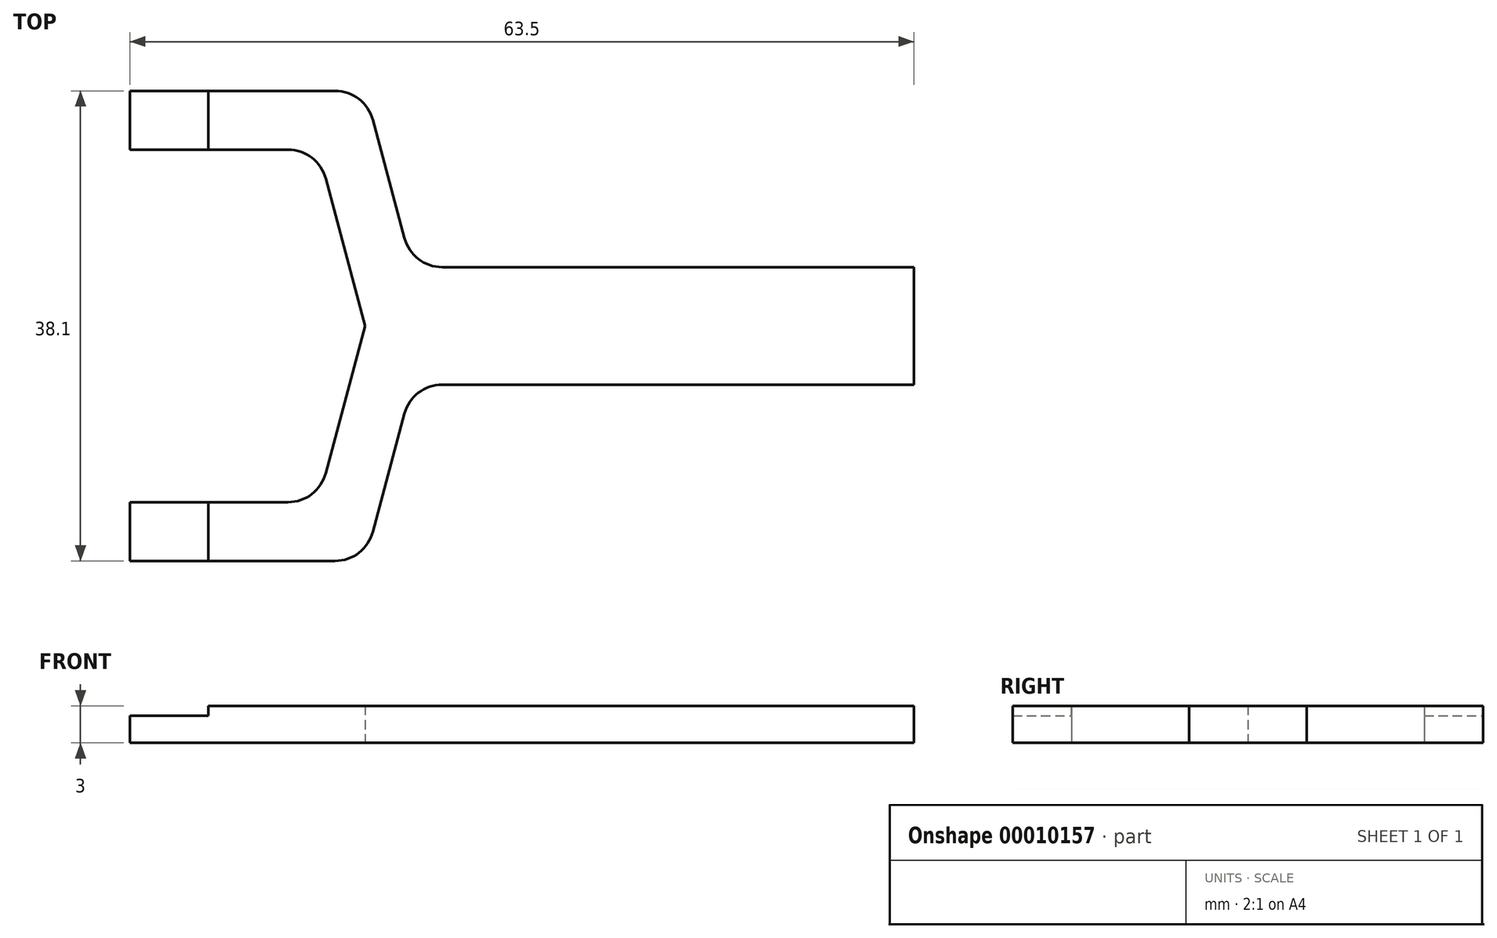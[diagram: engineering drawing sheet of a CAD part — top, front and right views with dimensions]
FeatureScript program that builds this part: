
annotation { "Feature Type Name" : "Feature", "Feature Type Description" : "" }
export const myFeature = defineFeature(function(context is Context, id is Id, definition is map)
    precondition{}
    {
        {
            var Q0;
            Q0=qCreatedBy(makeId("Top.planeOp"),FACE);
            var sketch = newSketch(context, id + "F0", { "sketchPlane" : qUnion([Q0])});
            skLineSegment(sketch, "E0", {"start": v(-19.05, 19.05) * mm, "end": v(-2.44, 19.05) * mm});
            skLineSegment(sketch, "E1", {"start": v(0.63, 16.7) * mm, "end": v(3.18, 7.12) * mm});
            skLineSegment(sketch, "E2", {"start": v(6.25, 4.76) * mm, "end": v(44.45, 4.76) * mm});
            skLineSegment(sketch, "E3", {"start": v(44.45, 4.76) * mm, "end": v(44.45, 0) * mm});
            skLineSegment(sketch, "E4", {"start": v(44.45, 0) * mm, "end": v(0, 0) * mm});
            skLineSegment(sketch, "E5", {"start": v(-19.05, 19.05) * mm, "end": v(-19.05, 14.29) * mm});
            skLineSegment(sketch, "E6", {"start": v(-19.05, 14.29) * mm, "end": v(-6.25, 14.29) * mm});
            skLineSegment(sketch, "E7", {"start": v(-3.18, 11.93) * mm, "end": v(0, 0) * mm});
            skPoint(sketch, "E8.visualSharp", {"position": v(3.81, 4.76) * mm});
            skArc(sketch, "E8.filletArc", {"start": v(3.18, 7.12) * mm, "mid": v(4.31, 5.42) * mm, "end": v(6.25, 4.76) * mm});
            skPoint(sketch, "E9.visualSharp", {"position": v(0, 19.05) * mm});
            skArc(sketch, "E9.filletArc", {"start": v(0.63, 16.7) * mm, "mid": v(-0.5, 18.4) * mm, "end": v(-2.44, 19.05) * mm});
            skPoint(sketch, "E10.visualSharp", {"position": v(-3.81, 14.29) * mm});
            skArc(sketch, "E10.filletArc", {"start": v(-3.18, 11.93) * mm, "mid": v(-4.31, 13.63) * mm, "end": v(-6.25, 14.29) * mm});
            skLineSegment(sketch, "E11", {"start": v(44.45, 0) * mm, "end": v(-26.71, 0) * mm, "construction": true});
            skSolve(sketch);
        }
        {
            var Q0;
            Q0=makeQuery(id+"F0.imprint","IMPRINT",FACE,{"disambiguationData":[TD([[makeQuery(id+"F0.imprint","IMPRINT",EDGE,{"derivedFrom":sQuery(id+"F0.wireOp",EDGE,"E0")}),-1.0]])]});
            extrude(context, id + "F1", {"entities" : qUnion([Q0]), "depth" : 3 * mm});
        }
        {
            var Q0;
            Q0=makeQuery(id+"F1.opExtrude","SWEPT_BODY",BODY,{"disambiguationData":[OSD([sQuery(id+"F0.wireOp",EDGE,"E0"),sQuery(id+"F0.wireOp",EDGE,"E1"),sQuery(id+"F0.wireOp",EDGE,"E2"),sQuery(id+"F0.wireOp",EDGE,"E3"),sQuery(id+"F0.wireOp",EDGE,"E4"),sQuery(id+"F0.wireOp",EDGE,"E5"),sQuery(id+"F0.wireOp",EDGE,"E6"),sQuery(id+"F0.wireOp",EDGE,"E7"),sQuery(id+"F0.wireOp",EDGE,"E8.filletArc"),sQuery(id+"F0.wireOp",EDGE,"E9.filletArc"),sQuery(id+"F0.wireOp",EDGE,"E10.filletArc")])]});
            var Q1;
            Q1=qCreatedBy(makeId("Front.planeOp"),FACE);
            mirror(context, id + "F2", {"operationType" : NewBodyOperationType.ADD, "entities" : qUnion([Q0]), "mirrorPlane" : qUnion([Q1])});
        }
        {
            var Q0;
            {var subQ0=makeQuery(id+"F1.opExtrude","CAP_FACE",FACE,{"disambiguationData":[OSD([sQuery(id+"F0.wireOp",EDGE,"E0"),sQuery(id+"F0.wireOp",EDGE,"E1"),sQuery(id+"F0.wireOp",EDGE,"E2"),sQuery(id+"F0.wireOp",EDGE,"E3"),sQuery(id+"F0.wireOp",EDGE,"E4"),sQuery(id+"F0.wireOp",EDGE,"E5"),sQuery(id+"F0.wireOp",EDGE,"E6"),sQuery(id+"F0.wireOp",EDGE,"E7"),sQuery(id+"F0.wireOp",EDGE,"E8.filletArc"),sQuery(id+"F0.wireOp",EDGE,"E9.filletArc"),sQuery(id+"F0.wireOp",EDGE,"E10.filletArc")])],"isStart":false});Q0=makeQuery(id+"F2.boolean.opBoolean","MERGE",FACE,{"derivedFrom":[subQ0,makeQuery(id+"F2.opPattern","COPY",FACE,{"derivedFrom":subQ0,"instanceName":"1"})]});}
            var sketch = newSketch(context, id + "F3", { "sketchPlane" : qUnion([Q0])});
            skLineSegment(sketch, "E12.bottom", {"start": v(-12.7, -19.05) * mm, "end": v(-19.05, -19.05) * mm});
            skLineSegment(sketch, "E12.top", {"start": v(-12.7, 19.05) * mm, "end": v(-19.05, 19.05) * mm});
            skLineSegment(sketch, "E12.left", {"start": v(-12.7, -19.05) * mm, "end": v(-12.7, 19.05) * mm});
            skLineSegment(sketch, "E12.right", {"start": v(-19.05, -19.05) * mm, "end": v(-19.05, 19.05) * mm});
            skSolve(sketch);
        }
        {
            var Q0;
            Q0 = qSketchRegion(id + "F3", true);
            extrude(context, id + "F4", {"entities" : qUnion([Q0]), "operationType" : NewBodyOperationType.REMOVE, "oppositeDirection" : true, "depth" : .8 * mm});
        }
    });
